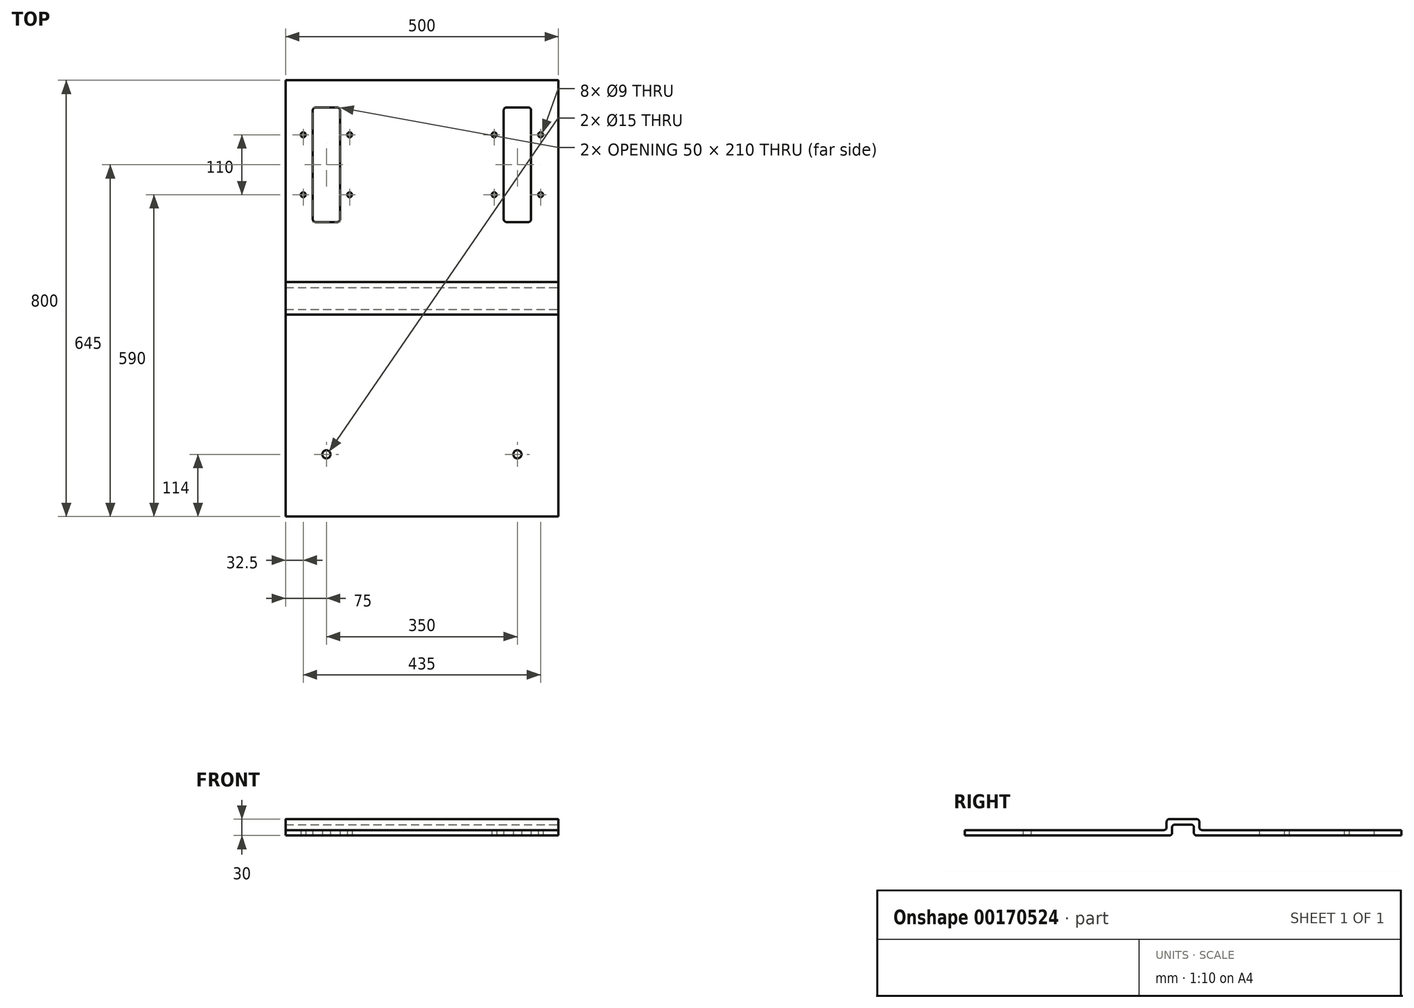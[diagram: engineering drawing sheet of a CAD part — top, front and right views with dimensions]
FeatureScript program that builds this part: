
annotation { "Feature Type Name" : "Feature", "Feature Type Description" : "" }
export const myFeature = defineFeature(function(context is Context, id is Id, definition is map)
    precondition{}
    {
        {
            var Q0;
            Q0=qCreatedBy(makeId("Top.planeOp"),FACE);
            var sketch = newSketch(context, id + "F0", { "sketchPlane" : qUnion([Q0])});
            skLineSegment(sketch, "E0.bottom", {"start": v(-250, 225) * mm, "end": v(250, 225) * mm});
            skLineSegment(sketch, "E0.top", {"start": v(-250, -575) * mm, "end": v(250, -575) * mm});
            skLineSegment(sketch, "E0.left", {"start": v(-250, 225) * mm, "end": v(-250, -575) * mm});
            skLineSegment(sketch, "E0.right", {"start": v(250, 225) * mm, "end": v(250, -575) * mm});
            skLineSegment(sketch, "E1", {"start": v(0, 225) * mm, "end": v(0, -281.03) * mm, "construction": true});
            skLineSegment(sketch, "E2", {"start": v(250, 0) * mm, "end": v(-550, 0) * mm, "construction": true});
            skLineSegment(sketch, "E3.bottom", {"start": v(-195, 175) * mm, "end": v(-155, 175) * mm});
            skLineSegment(sketch, "E3.top", {"start": v(-195, -35) * mm, "end": v(-155, -35) * mm});
            skLineSegment(sketch, "E3.left", {"start": v(-200, 170) * mm, "end": v(-200, -30) * mm});
            skLineSegment(sketch, "E3.right", {"start": v(-150, 170) * mm, "end": v(-150, -30) * mm});
            skCircle(sketch, "E4", {"center": v(-217.5, 125) * mm, "radius": 4.5 * mm});
            skLineSegment(sketch, "E5", {"start": v(-200, 70) * mm, "end": v(-239.44, 70) * mm, "construction": true});
            skLineSegment(sketch, "E6", {"start": v(-175, 175) * mm, "end": v(-175, -66.2) * mm, "construction": true});
            skCircle(sketch, "E7.MirrorC", {"center": v(-217.5, 15) * mm, "radius": 4.5 * mm});
            skCircle(sketch, "E8.MirrorC", {"center": v(-132.5, 125) * mm, "radius": 4.5 * mm});
            skCircle(sketch, "E9.MirrorC", {"center": v(-132.5, 15) * mm, "radius": 4.5 * mm});
            skPoint(sketch, "E10.visualSharp", {"position": v(-200, 175) * mm});
            skArc(sketch, "E10.filletArc", {"start": v(-195, 175) * mm, "mid": v(-198.54, 173.54) * mm, "end": v(-200, 170) * mm});
            skPoint(sketch, "E11.visualSharp", {"position": v(-150, 175) * mm});
            skArc(sketch, "E11.filletArc", {"start": v(-150, 170) * mm, "mid": v(-151.46, 173.54) * mm, "end": v(-155, 175) * mm});
            skPoint(sketch, "E12.visualSharp", {"position": v(-200, -35) * mm});
            skArc(sketch, "E12.filletArc", {"start": v(-200, -30) * mm, "mid": v(-198.54, -33.54) * mm, "end": v(-195, -35) * mm});
            skPoint(sketch, "E13.visualSharp", {"position": v(-150, -35) * mm});
            skArc(sketch, "E13.filletArc", {"start": v(-155, -35) * mm, "mid": v(-151.46, -33.54) * mm, "end": v(-150, -30) * mm});
            skArc(sketch, "E14.MirrorCS", {"start": v(155, -35) * mm, "mid": v(151.46, -33.54) * mm, "end": v(150, -30) * mm});
            skArc(sketch, "E15.MirrorCS", {"start": v(150, 170) * mm, "mid": v(151.46, 173.54) * mm, "end": v(155, 175) * mm});
            skArc(sketch, "E16.MirrorCS", {"start": v(200, -30) * mm, "mid": v(198.54, -33.54) * mm, "end": v(195, -35) * mm});
            skArc(sketch, "E17.MirrorCS", {"start": v(195, 175) * mm, "mid": v(198.54, 173.54) * mm, "end": v(200, 170) * mm});
            skCircle(sketch, "E18.MirrorC", {"center": v(217.5, 15) * mm, "radius": 4.5 * mm});
            skCircle(sketch, "E19.MirrorC", {"center": v(132.5, 125) * mm, "radius": 4.5 * mm});
            skCircle(sketch, "E20.MirrorC", {"center": v(132.5, 15) * mm, "radius": 4.5 * mm});
            skCircle(sketch, "E21.MirrorC", {"center": v(217.5, 125) * mm, "radius": 4.5 * mm});
            skPoint(sketch, "E22.MirrorP", {"position": v(200, -35) * mm});
            skLineSegment(sketch, "E23.MirrorCS", {"start": v(195, 175) * mm, "end": v(155, 175) * mm});
            skLineSegment(sketch, "E24.MirrorCS", {"start": v(195, -35) * mm, "end": v(155, -35) * mm});
            skPoint(sketch, "E25.MirrorP", {"position": v(150, -35) * mm});
            skPoint(sketch, "E26.MirrorP", {"position": v(150, 175) * mm});
            skLineSegment(sketch, "E27.MirrorCS", {"start": v(200, 170) * mm, "end": v(200, -30) * mm});
            skLineSegment(sketch, "E28.MirrorCS", {"start": v(150, 170) * mm, "end": v(150, -30) * mm});
            skPoint(sketch, "E29.MirrorP", {"position": v(200, 175) * mm});
            skLineSegment(sketch, "E30", {"start": v(-175, -428.1) * mm, "end": v(-175, -642.63) * mm, "construction": true});
            skCircle(sketch, "E31", {"center": v(-175, -461) * mm, "radius": 7.5 * mm});
            skCircle(sketch, "E32.MirrorC", {"center": v(175, -461) * mm, "radius": 7.5 * mm});
            skSolve(sketch);
        }
        {
            var Q0;
            Q0=makeQuery(id+"F0.imprint","IMPRINT",FACE,{"disambiguationData":[TD([[makeQuery(id+"F0.imprint","IMPRINT",EDGE,{"derivedFrom":sQuery(id+"F0.wireOp",EDGE,"E0.bottom")}),-1.0]])]});
            extrude(context, id + "F1", {"entities" : qUnion([Q0]), "depth" : 10 * mm});
        }
        {
            var Q0;
            Q0=makeQuery(id+"F1.opExtrude","SWEPT_FACE",FACE,{"disambiguationData":[OSD([sQuery(id+"F0.wireOp",EDGE,"E0.right")])]});
            var sketch = newSketch(context, id + "F2", { "sketchPlane" : qUnion([Q0])});
            skLineSegment(sketch, "E33", {"start": v(-175, 10) * mm, "end": v(-175, 114.72) * mm, "construction": true});
            skLineSegment(sketch, "E34.top", {"start": v(-200, 30) * mm, "end": v(-150, 30) * mm});
            skLineSegment(sketch, "E34.left", {"start": v(-205, 15) * mm, "end": v(-205, 25) * mm});
            skLineSegment(sketch, "E34.right", {"start": v(-145, 15) * mm, "end": v(-145, 25) * mm});
            skPoint(sketch, "E35.visualSharp", {"position": v(-205, 30) * mm});
            skArc(sketch, "E35.filletArc", {"start": v(-200, 30) * mm, "mid": v(-203.54, 28.54) * mm, "end": v(-205, 25) * mm});
            skPoint(sketch, "E36.visualSharp", {"position": v(-145, 30) * mm});
            skArc(sketch, "E36.filletArc", {"start": v(-145, 25) * mm, "mid": v(-146.46, 28.54) * mm, "end": v(-150, 30) * mm});
            skLineSegment(sketch, "E37.0", {"start": v(-190, 20) * mm, "end": v(-160, 20) * mm});
            skLineSegment(sketch, "E38.0", {"start": v(-195, 10) * mm, "end": v(-195, 15) * mm});
            skLineSegment(sketch, "E39.0", {"start": v(-155, 10) * mm, "end": v(-155, 15) * mm});
            skArc(sketch, "E40.filletArc", {"start": v(-190, 20) * mm, "mid": v(-193.54, 18.54) * mm, "end": v(-195, 15) * mm});
            skArc(sketch, "E41.filletArc", {"start": v(-155, 15) * mm, "mid": v(-156.46, 18.54) * mm, "end": v(-160, 20) * mm});
            skLineSegment(sketch, "E42.bottom", {"start": v(-218.86, 0) * mm, "end": v(-132.59, 0) * mm});
            skLineSegment(sketch, "E42.top", {"start": v(-218.86, 10) * mm, "end": v(-210, 10) * mm});
            skLineSegment(sketch, "E42.left", {"start": v(-218.86, 0) * mm, "end": v(-218.86, 10) * mm});
            skLineSegment(sketch, "E42.right", {"start": v(-132.59, 0) * mm, "end": v(-132.59, 10) * mm});
            skLineSegment(sketch, "E43.trimOffspring", {"start": v(-140, 10) * mm, "end": v(-132.59, 10) * mm});
            skPoint(sketch, "E44.visualSharp", {"position": v(-205, 10) * mm});
            skArc(sketch, "E44.filletArc", {"start": v(-210, 10) * mm, "mid": v(-206.46, 11.46) * mm, "end": v(-205, 15) * mm});
            skPoint(sketch, "E45.visualSharp", {"position": v(-145, 10) * mm});
            skArc(sketch, "E45.filletArc", {"start": v(-145, 15) * mm, "mid": v(-143.54, 11.46) * mm, "end": v(-140, 10) * mm});
            skLineSegment(sketch, "E46", {"start": v(-195, 10) * mm, "end": v(-195, 0) * mm});
            skLineSegment(sketch, "E47", {"start": v(-155, 10) * mm, "end": v(-155, 0) * mm});
            skLineSegment(sketch, "E48", {"start": v(-155, 0) * mm, "end": v(-195, 0) * mm});
            skSolve(sketch);
        }
        {
            var Q0;
            Q0=makeQuery(id+"F2.imprint","IMPRINT",FACE,{"disambiguationData":[TD([[makeQuery(id+"F2.imprint","IMPRINT",EDGE,{"derivedFrom":sQuery(id+"F2.wireOp",EDGE,"E34.top")}),-1.0]])]});
            var Q1;
            Q1=makeQuery(id+"F1.opExtrude","SWEPT_FACE",FACE,{"disambiguationData":[OSD([sQuery(id+"F0.wireOp",EDGE,"E0.left")])]});
            extrude(context, id + "F3", {"entities" : qUnion([Q0]), "operationType" : NewBodyOperationType.ADD, "endBound" : BoundingType.UP_TO_SURFACE, "oppositeDirection" : true, "endBoundEntityFace" : qUnion([Q1]), "depth" : 25 * mm});
        }
        {
            var Q0;
            {var subQ0=sQuery(id+"F0.wireOp",EDGE,"E0.right");Q0=makeQuery(id+"F3.boolean.opBoolean","MERGE",FACE,{"derivedFrom":[makeQuery(id+"F1.opExtrude","SWEPT_FACE",FACE,{"disambiguationData":[OSD([subQ0])]}),makeQuery(id+"F3.opExtrude","CAP_FACE",FACE,{"disambiguationData":[OSD([subQ0,sQuery(id+"F2.wireOp",EDGE,"E34.top"),sQuery(id+"F2.wireOp",EDGE,"E34.left"),sQuery(id+"F2.wireOp",EDGE,"E34.right"),sQuery(id+"F2.wireOp",EDGE,"E35.filletArc"),sQuery(id+"F2.wireOp",EDGE,"E36.filletArc"),sQuery(id+"F2.wireOp",EDGE,"E37.0"),sQuery(id+"F2.wireOp",EDGE,"E38.0"),sQuery(id+"F2.wireOp",EDGE,"E39.0"),sQuery(id+"F2.wireOp",EDGE,"E40.filletArc"),sQuery(id+"F2.wireOp",EDGE,"E41.filletArc"),sQuery(id+"F2.wireOp",EDGE,"E44.filletArc"),sQuery(id+"F2.wireOp",EDGE,"E45.filletArc")])],"isStart":true})]});}
            var sketch = newSketch(context, id + "F4", { "sketchPlane" : qUnion([Q0])});
            skLineSegment(sketch, "E49.bottom", {"start": v(-195, 10) * mm, "end": v(-155, 10) * mm});
            skLineSegment(sketch, "E49.left", {"start": v(-195, 10) * mm, "end": v(-195, 5) * mm});
            skLineSegment(sketch, "E49.right", {"start": v(-155, 10) * mm, "end": v(-155, 5) * mm});
            skLineSegment(sketch, "E50.bottom", {"start": v(-211.01, 0) * mm, "end": v(-200, 0) * mm});
            skLineSegment(sketch, "E50.top", {"start": v(-211.01, -10.53) * mm, "end": v(-138.86, -10.53) * mm});
            skLineSegment(sketch, "E50.left", {"start": v(-211.01, 0) * mm, "end": v(-211.01, -10.53) * mm});
            skLineSegment(sketch, "E50.right", {"start": v(-138.86, 0) * mm, "end": v(-138.86, -10.53) * mm});
            skArc(sketch, "E51.filletArc", {"start": v(-200, 0) * mm, "mid": v(-196.46, 1.46) * mm, "end": v(-195, 5) * mm});
            skLineSegment(sketch, "E52", {"start": v(-150, 0) * mm, "end": v(-138.86, 0) * mm});
            skPoint(sketch, "E53.visualSharp", {"position": v(-155, 0) * mm});
            skArc(sketch, "E53.filletArc", {"start": v(-155, 5) * mm, "mid": v(-153.54, 1.46) * mm, "end": v(-150, 0) * mm});
            skSolve(sketch);
        }
        {
            var Q0;
            {var subQ0=sQuery(id+"F4.wireOp",EDGE,"E50.bottom");Q0=makeQuery(id+"F4.imprint","IMPRINT",FACE,{"disambiguationData":[TD([[makeQuery(id+"F4.imprint","IMPRINT",EDGE,{"derivedFrom":subQ0}),1.0]])]});}
            var Q1;
            Q1=makeQuery(id+"F4.imprint","IMPRINT",FACE,{"disambiguationData":[TD([[makeQuery(id+"F4.imprint","IMPRINT",EDGE,{"derivedFrom":sQuery(id+"F4.wireOp",EDGE,"E49.bottom")}),1.0]])]});
            extrude(context, id + "F5", {"entities" : qUnion([Q0, Q1]), "operationType" : NewBodyOperationType.REMOVE, "endBound" : BoundingType.THROUGH_ALL, "oppositeDirection" : true, "depth" : 25 * mm});
        }
    });
